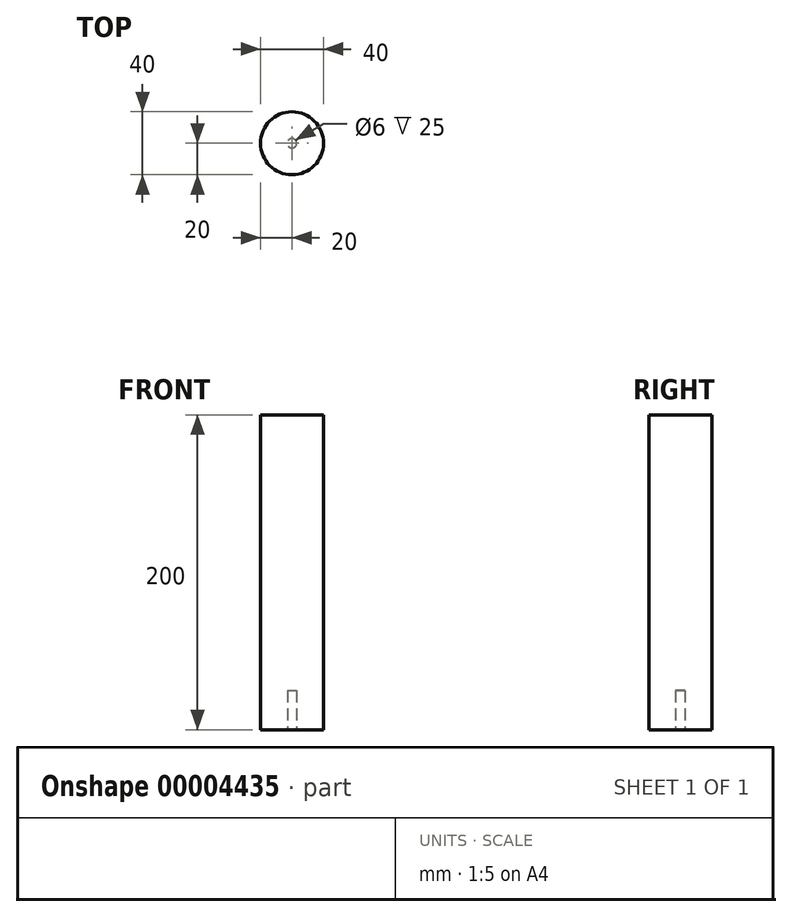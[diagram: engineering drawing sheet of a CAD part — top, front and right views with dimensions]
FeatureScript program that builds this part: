
annotation { "Feature Type Name" : "Feature", "Feature Type Description" : "" }
export const myFeature = defineFeature(function(context is Context, id is Id, definition is map)
    precondition{}
    {
        {
            var Q0;
            Q0=qCreatedBy(makeId("Top.planeOp"),FACE);
            var sketch = newSketch(context, id + "F0", { "sketchPlane" : qUnion([Q0])});
            skCircle(sketch, "E0", {"center": v(0, 0) * mm, "radius": 20 * mm});
            skSolve(sketch);
        }
        {
            var Q0;
            Q0=makeQuery(id+"F0.imprint","IMPRINT",FACE,{"disambiguationData":[TD([[makeQuery(id+"F0.imprint","IMPRINT",EDGE,{"derivedFrom":sQuery(id+"F0.wireOp",EDGE,"E0")}),1.0]])]});
            extrude(context, id + "F1", {"entities" : qUnion([Q0]), "depth" : 200 * mm});
        }
        {
            var Q0;
            Q0=makeQuery(id+"F1.opExtrude","CAP_FACE",FACE,{"disambiguationData":[OSD([sQuery(id+"F0.wireOp",EDGE,"E0")])],"isStart":true});
            var sketch = newSketch(context, id + "F2", { "sketchPlane" : qUnion([Q0])});
            skCircle(sketch, "E1", {"center": v(0, 0) * mm, "radius": 3 * mm});
            skSolve(sketch);
        }
        {
            var Q0;
            Q0=makeQuery(id+"F2.imprint","IMPRINT",FACE,{"disambiguationData":[TD([[makeQuery(id+"F2.imprint","IMPRINT",EDGE,{"derivedFrom":sQuery(id+"F2.wireOp",EDGE,"E1")}),1.0]])]});
            extrude(context, id + "F3", {"entities" : qUnion([Q0]), "operationType" : NewBodyOperationType.REMOVE, "oppositeDirection" : true, "depth" : 25 * mm});
        }
    });
